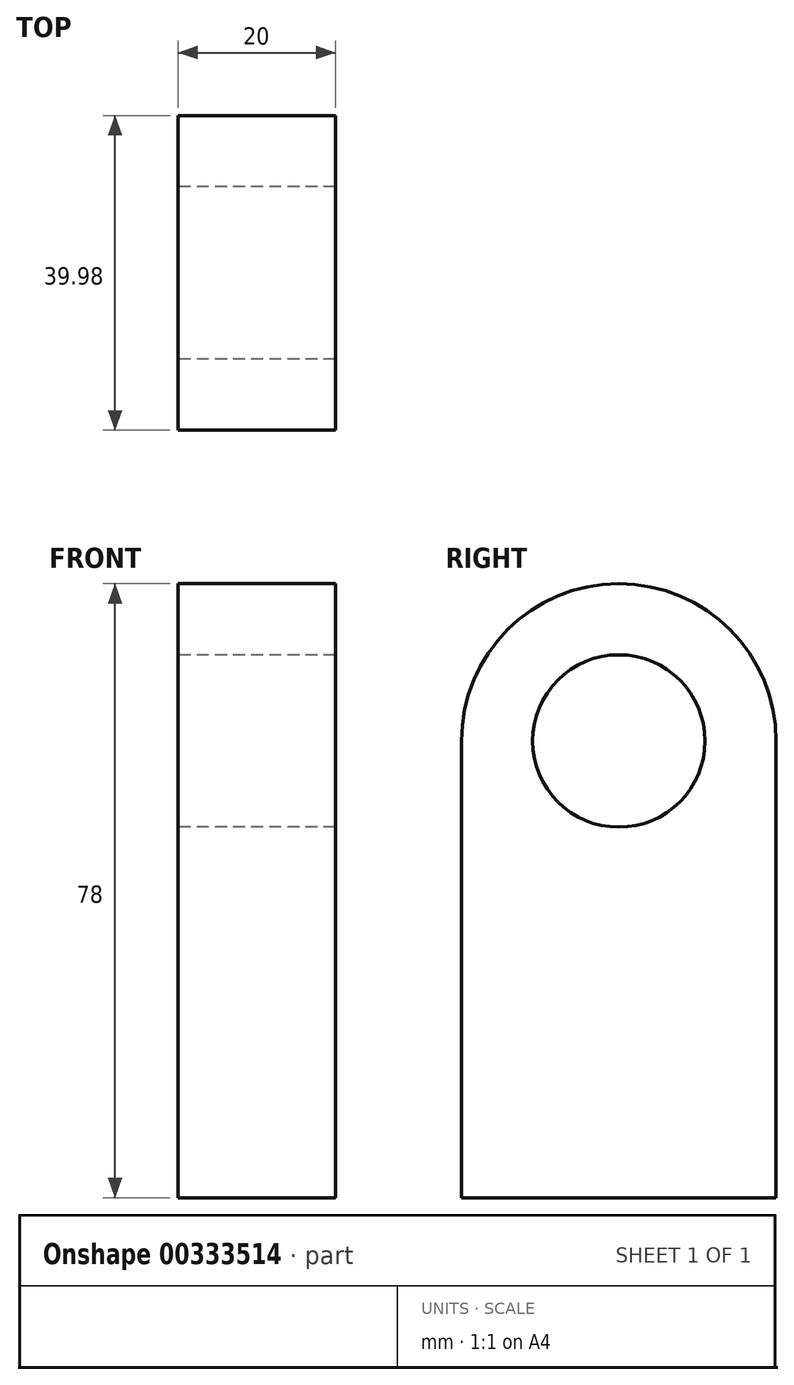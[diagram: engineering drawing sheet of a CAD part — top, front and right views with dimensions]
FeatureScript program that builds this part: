
annotation { "Feature Type Name" : "Feature", "Feature Type Description" : "" }
export const myFeature = defineFeature(function(context is Context, id is Id, definition is map)
    precondition{}
    {
        {
            var Q0;
            Q0=qCreatedBy(makeId("Right.planeOp"),FACE);
            var sketch = newSketch(context, id + "F0", { "sketchPlane" : qUnion([Q0])});
            skLineSegment(sketch, "E0.top", {"start": v(19.99, -29) * mm, "end": v(-19.99, -29) * mm});
            skLineSegment(sketch, "E0.left", {"start": v(19.99, 29) * mm, "end": v(19.99, -29) * mm});
            skLineSegment(sketch, "E0.right", {"start": v(-19.99, 29) * mm, "end": v(-19.99, -29) * mm});
            skPoint(sketch, "E0.middle", {"position": v(0, 0) * mm});
            skArc(sketch, "E1", {"start": v(-19.99, 29) * mm, "mid": v(0, 49) * mm, "end": v(19.99, 29) * mm});
            skCircle(sketch, "E2", {"center": v(0, 29) * mm, "radius": 10.95 * mm});
            skSolve(sketch);
        }
        {
            var Q0;
            Q0=makeQuery(id+"F0.imprint","IMPRINT",FACE,{"disambiguationData":[TD([[makeQuery(id+"F0.imprint","IMPRINT",EDGE,{"derivedFrom":sQuery(id+"F0.wireOp",EDGE,"E0.top")}),-1.0]])]});
            extrude(context, id + "F1", {"entities" : qUnion([Q0]), "depth" : 20 * mm, "offsetDistance" : 25 * mm});
        }
    });
